# Revit family: BX4-12
name_source: partatom
category: Lighting Fixtures
revit_build: Autodesk Revit 2014 (Build: 20130308_1515(x64)
units: mm (PartAtom-declared; Revit-internal decimal feet)

## types (1)
- BX4-12
    Apparent Load = 0 VA
    Assembly Code = D5020220
    Backbox = Aluminum housing
    Baffle = Hubbell - White
    Baffle Type = Baffle : TA12C
    Color Filter = 16777215
    Default Elevation = 48.000"
    Description = 4'' Low Voltage Incandescent Downlight
    Dimming Lamp Color Temperature Shift = <None>
    Lamp = INC
    Load Classification = Lighting
    Manufacturer = Prescolite
    Model = BX4-12
    Photometric Web File = generic
    Power Factor = 1
    Product Documentation Link = http://www.prescolite.com
    Product Page URL = http://www.prescolite.com
    Reflector = Hubbell - Black
    Tilt Angle = -90.00°
    URL = https://www.hubbell.com
    Voltage = 120 V

## geometry (parser evidence)
native form markers: Blend x8, Sweep x4
no freeform markers — native parametric forms only
